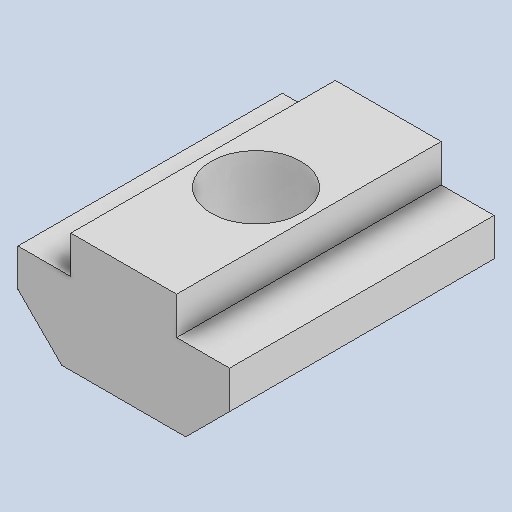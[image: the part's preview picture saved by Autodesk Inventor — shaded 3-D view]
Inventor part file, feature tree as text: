
AUTODESK INVENTOR PART (.ipt)
format: ipt  version: 2022 (Build 260153000, 153)  size: 100,352 bytes
history: native  units: in
note: dims shown in document units (in); Inventor stores cm internally (conversion verified against a paired STEP export)
features: hole x1
ambient origin geometry x8: Origin, YZ Plane, XZ Plane, XY Plane, X Axis, Y Axis, Z Axis, Center Point
bodies: Solid1 (feature_tree)
feature tree (1):
  hole  "Hole2"  [1 undecoded]
note: 1 required parameter value undecoded (feature->parameter linkage not recoverable at this tier; creation-order binding heuristic only, values carry confidence <= 0.55)
